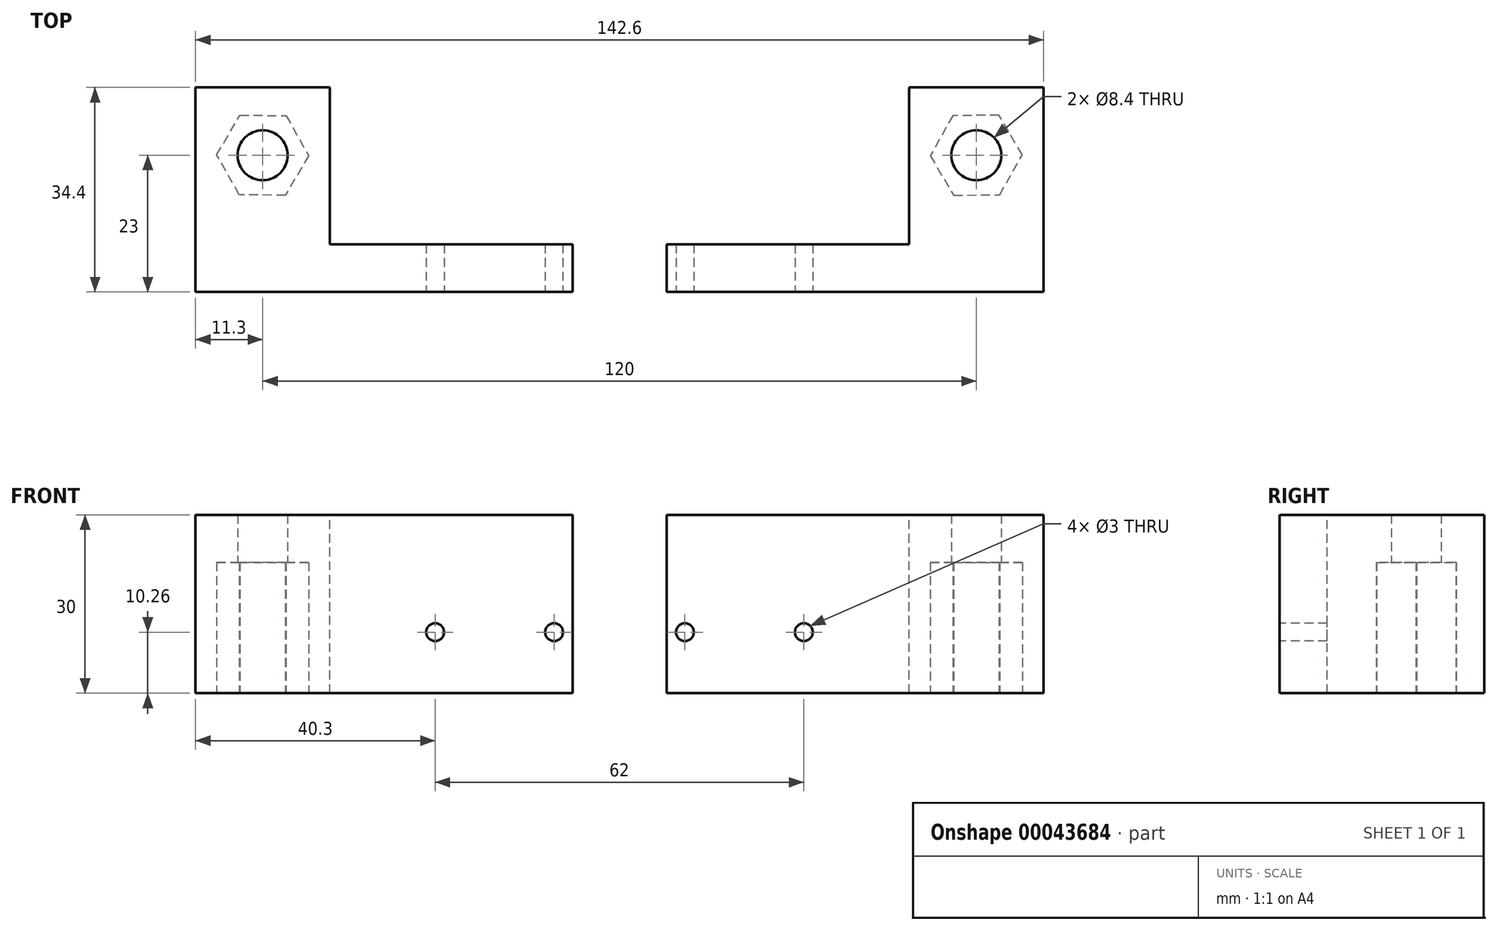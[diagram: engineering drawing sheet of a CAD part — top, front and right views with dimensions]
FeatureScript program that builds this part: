
annotation { "Feature Type Name" : "Feature", "Feature Type Description" : "" }
export const myFeature = defineFeature(function(context is Context, id is Id, definition is map)
    precondition{}
    {
        {
            var Q0;
            Q0=qCreatedBy(makeId("Front.planeOp"),FACE);
            var sketch = newSketch(context, id + "F0", { "sketchPlane" : qUnion([Q0])});
            skLineSegment(sketch, "E0.rect.bottom", {"start": v(31.7, 15) * mm, "end": v(-31.7, 15) * mm});
            skLineSegment(sketch, "E0.rect.top", {"start": v(31.7, -15) * mm, "end": v(-31.7, -15) * mm});
            skLineSegment(sketch, "E0.rect.left", {"start": v(31.7, 15) * mm, "end": v(31.7, -15) * mm});
            skLineSegment(sketch, "E0.rect.right", {"start": v(-31.7, 15) * mm, "end": v(-31.7, -15) * mm});
            skPoint(sketch, "E0.rect.middle", {"position": v(0, 0) * mm});
            skSolve(sketch);
        }
        {
            var Q0;
            Q0 = qSketchRegion(id + "F0", true);
            extrude(context, id + "F1", {"entities" : qUnion([Q0]), "endBound" : BoundingType.SYMMETRIC, "depth" : 8 * mm});
        }
        {
            var Q0;
            Q0=makeQuery(id+"F1.opExtrude","CAP_FACE",FACE,{"disambiguationData":[OSD([sQuery(id+"F0.wireOp",EDGE,"E0.rect.bottom"),sQuery(id+"F0.wireOp",EDGE,"E0.rect.top"),sQuery(id+"F0.wireOp",EDGE,"E0.rect.left"),sQuery(id+"F0.wireOp",EDGE,"E0.rect.right")])],"isStart":false});
            var sketch = newSketch(context, id + "F2", { "sketchPlane" : qUnion([Q0])});
            skPoint(sketch, "E1", {"position": v(-28.6, -4.74) * mm});
            skPoint(sketch, "E2", {"position": v(-8.6, -4.74) * mm});
            skLineSegment(sketch, "E3", {"start": v(-5.6, 15) * mm, "end": v(-5.6, -15) * mm, "construction": true});
            skLineSegment(sketch, "E4", {"start": v(20.4, 15) * mm, "end": v(20.4, -15) * mm, "construction": true});
            skSolve(sketch);
        }
        {
            var Q0;
            Q0=sQuery(id+"F2.wireOp",VERTEX,"E1");
            var Q1;
            Q1=sQuery(id+"F2.wireOp",VERTEX,"E2");
            var Q2;
            Q2=makeQuery(id+"F1.opExtrude","SWEPT_BODY",BODY,{"disambiguationData":[OSD([sQuery(id+"F0.wireOp",EDGE,"E0.rect.bottom"),sQuery(id+"F0.wireOp",EDGE,"E0.rect.top"),sQuery(id+"F0.wireOp",EDGE,"E0.rect.left"),sQuery(id+"F0.wireOp",EDGE,"E0.rect.right")])]});
            hole(context, id + "F3", {"style" : HoleStyle.SIMPLE, "holeDiameter" : 3 * mm, "endStyle" : HoleEndStyle.THROUGH, "locations" : qUnion([Q0, Q1]), "scope" : qUnion([Q2])});
        }
        {
            var Q0;
            Q0=makeQuery(id+"F1.opExtrude","SWEPT_FACE",FACE,{"disambiguationData":[OSD([sQuery(id+"F0.wireOp",EDGE,"E0.rect.left")])]});
            var Q1;
            Q1=sQuery(id+"F2.wireOp",VERTEX,"E4.start");
            cPlane(context, id + "F4", {"entities" : qUnion([Q0, Q1]), "cplaneType" : CPlaneType.PLANE_POINT, "offset" : 150 * mm, "width" : 150 * mm, "height" : 150 * mm});
        }
        {
            var Q0;
            Q0=qCreatedBy(id+"F4.planeOp",FACE);
            var sketch = newSketch(context, id + "F5", { "sketchPlane" : qUnion([Q0])});
            skLineSegment(sketch, "E5.bottom", {"start": v(30.4, -15) * mm, "end": v(-4, -15) * mm});
            skLineSegment(sketch, "E5.top", {"start": v(30.4, 15) * mm, "end": v(-4, 15) * mm});
            skLineSegment(sketch, "E5.left", {"start": v(30.4, -15) * mm, "end": v(30.4, 15) * mm});
            skLineSegment(sketch, "E5.right", {"start": v(-4, -15) * mm, "end": v(-4, 15) * mm});
            skSolve(sketch);
        }
        {
            var Q0;
            Q0=makeQuery(id+"F5.imprint","IMPRINT",FACE,{"disambiguationData":[TD([[makeQuery(id+"F5.imprint","IMPRINT",EDGE,{"derivedFrom":sQuery(id+"F5.wireOp",EDGE,"E5.bottom")}),-1.0]])]});
            extrude(context, id + "F6", {"entities" : qUnion([Q0]), "operationType" : NewBodyOperationType.ADD, "endBound" : BoundingType.SYMMETRIC, "depth" : 22.6 * mm});
        }
        {
            var Q0;
            Q0=makeQuery(id+"F6.boolean.opBoolean","MERGE",FACE,{"derivedFrom":[makeQuery(id+"F1.opExtrude","SWEPT_FACE",FACE,{"disambiguationData":[OSD([sQuery(id+"F0.wireOp",EDGE,"E0.rect.left")])]}),makeQuery(id+"F6.opExtrude","CAP_FACE",FACE,{"disambiguationData":[OSD([sQuery(id+"F5.wireOp",EDGE,"E5.bottom"),sQuery(id+"F5.wireOp",EDGE,"E5.top"),sQuery(id+"F5.wireOp",EDGE,"E5.left"),sQuery(id+"F5.wireOp",EDGE,"E5.right")])],"isStart":false})]});
            var sketch = newSketch(context, id + "F7", { "sketchPlane" : qUnion([Q0])});
            skLineSegment(sketch, "E6", {"start": v(19, 15) * mm, "end": v(19, -15) * mm, "construction": true});
            skSolve(sketch);
        }
        {
            var Q0;
            Q0=makeQuery(id+"F6.boolean.opBoolean","MERGE",FACE,{"derivedFrom":[makeQuery(id+"F1.opExtrude","SWEPT_FACE",FACE,{"disambiguationData":[OSD([sQuery(id+"F0.wireOp",EDGE,"E0.rect.bottom")])]}),makeQuery(id+"F6.opExtrude","SWEPT_FACE",FACE,{"disambiguationData":[OSD([sQuery(id+"F5.wireOp",EDGE,"E5.top")])]})]});
            var sketch = newSketch(context, id + "F8", { "sketchPlane" : qUnion([Q0])});
            skLineSegment(sketch, "E7", {"start": v(31.7, 19) * mm, "end": v(9.1, 19) * mm, "construction": true});
            skLineSegment(sketch, "E8", {"start": v(20.4, -4) * mm, "end": v(20.4, 30.4) * mm, "construction": true});
            skPoint(sketch, "E9", {"position": v(20.4, 19) * mm});
            skSolve(sketch);
        }
        {
            var Q0;
            Q0=makeQuery(id+"F6.boolean.opBoolean","MERGE",FACE,{"derivedFrom":[makeQuery(id+"F1.opExtrude","SWEPT_FACE",FACE,{"disambiguationData":[OSD([sQuery(id+"F0.wireOp",EDGE,"E0.rect.top")])]}),makeQuery(id+"F6.opExtrude","SWEPT_FACE",FACE,{"disambiguationData":[OSD([sQuery(id+"F5.wireOp",EDGE,"E5.bottom")])]})]});
            var sketch = newSketch(context, id + "F9", { "sketchPlane" : qUnion([Q0])});
            skPoint(sketch, "E10", {"position": v(20.4, -19) * mm});
            skSolve(sketch);
        }
        {
            var Q0;
            Q0=sQuery(id+"F9.wireOp",VERTEX,"E10");
            var Q1;
            Q1=makeQuery(id+"F1.opExtrude","SWEPT_BODY",BODY,{"disambiguationData":[OSD([sQuery(id+"F0.wireOp",EDGE,"E0.rect.bottom"),sQuery(id+"F0.wireOp",EDGE,"E0.rect.top"),sQuery(id+"F0.wireOp",EDGE,"E0.rect.left"),sQuery(id+"F0.wireOp",EDGE,"E0.rect.right")])]});
            hole(context, id + "F10", {"style" : HoleStyle.SIMPLE, "holeDiameter" : 8.4 * mm, "endStyle" : HoleEndStyle.THROUGH, "locations" : qUnion([Q0]), "scope" : qUnion([Q1])});
        }
        {
            var Q0;
            Q0=makeQuery(id+"F6.boolean.opBoolean","MERGE",FACE,{"derivedFrom":[makeQuery(id+"F1.opExtrude","SWEPT_FACE",FACE,{"disambiguationData":[OSD([sQuery(id+"F0.wireOp",EDGE,"E0.rect.top")])]}),makeQuery(id+"F6.opExtrude","SWEPT_FACE",FACE,{"disambiguationData":[OSD([sQuery(id+"F5.wireOp",EDGE,"E5.bottom")])]})]});
            var sketch = newSketch(context, id + "F11", { "sketchPlane" : qUnion([Q0])});
            skCircle(sketch, "E11.cCircle", {"center": v(20.4, -19) * mm, "radius": 6.7 * mm, "construction": true});
            skLineSegment(sketch, "E11.0", {"start": v(16.47, -25.67) * mm, "end": v(12.66, -18.93) * mm});
            skLineSegment(sketch, "E11.1", {"start": v(12.66, -18.93) * mm, "end": v(16.59, -12.27) * mm});
            skLineSegment(sketch, "E11.2", {"start": v(16.59, -12.27) * mm, "end": v(24.33, -12.33) * mm});
            skLineSegment(sketch, "E11.3", {"start": v(24.33, -12.33) * mm, "end": v(28.14, -19.07) * mm});
            skLineSegment(sketch, "E11.4", {"start": v(28.14, -19.07) * mm, "end": v(24.21, -25.73) * mm});
            skLineSegment(sketch, "E11.5", {"start": v(24.21, -25.73) * mm, "end": v(16.47, -25.67) * mm});
            skPoint(sketch, "E11.0.midPoint", {"position": v(14.57, -22.3) * mm});
            skSolve(sketch);
        }
        {
            var Q0;
            Q0=makeQuery(id+"F11.imprint","IMPRINT",FACE,{"disambiguationData":[TD([[makeQuery(id+"F11.imprint","IMPRINT",EDGE,{"derivedFrom":sQuery(id+"F11.wireOp",EDGE,"E11.0")}),-1.0]])]});
            extrude(context, id + "F12", {"entities" : qUnion([Q0]), "operationType" : NewBodyOperationType.REMOVE, "oppositeDirection" : true, "depth" : 22 * mm});
        }
        {
            var Q0;
            Q0=qCreatedBy(id+"F4.planeOp",FACE);
            cPlane(context, id + "F13", {"entities" : qUnion([Q0]), "cplaneType" : CPlaneType.OFFSET, "offset" : 60 * mm, "oppositeDirection" : true, "width" : 150 * mm, "height" : 150 * mm});
        }
        {
            var Q0;
            Q0=makeQuery(id+"F1.opExtrude","SWEPT_BODY",BODY,{"disambiguationData":[OSD([sQuery(id+"F0.wireOp",EDGE,"E0.rect.bottom"),sQuery(id+"F0.wireOp",EDGE,"E0.rect.top"),sQuery(id+"F0.wireOp",EDGE,"E0.rect.left"),sQuery(id+"F0.wireOp",EDGE,"E0.rect.right")])]});
            var Q1;
            Q1=qCreatedBy(id+"F13.planeOp",FACE);
            mirror(context, id + "F14", {"entities" : qUnion([Q0]), "mirrorPlane" : qUnion([Q1])});
        }
    });
